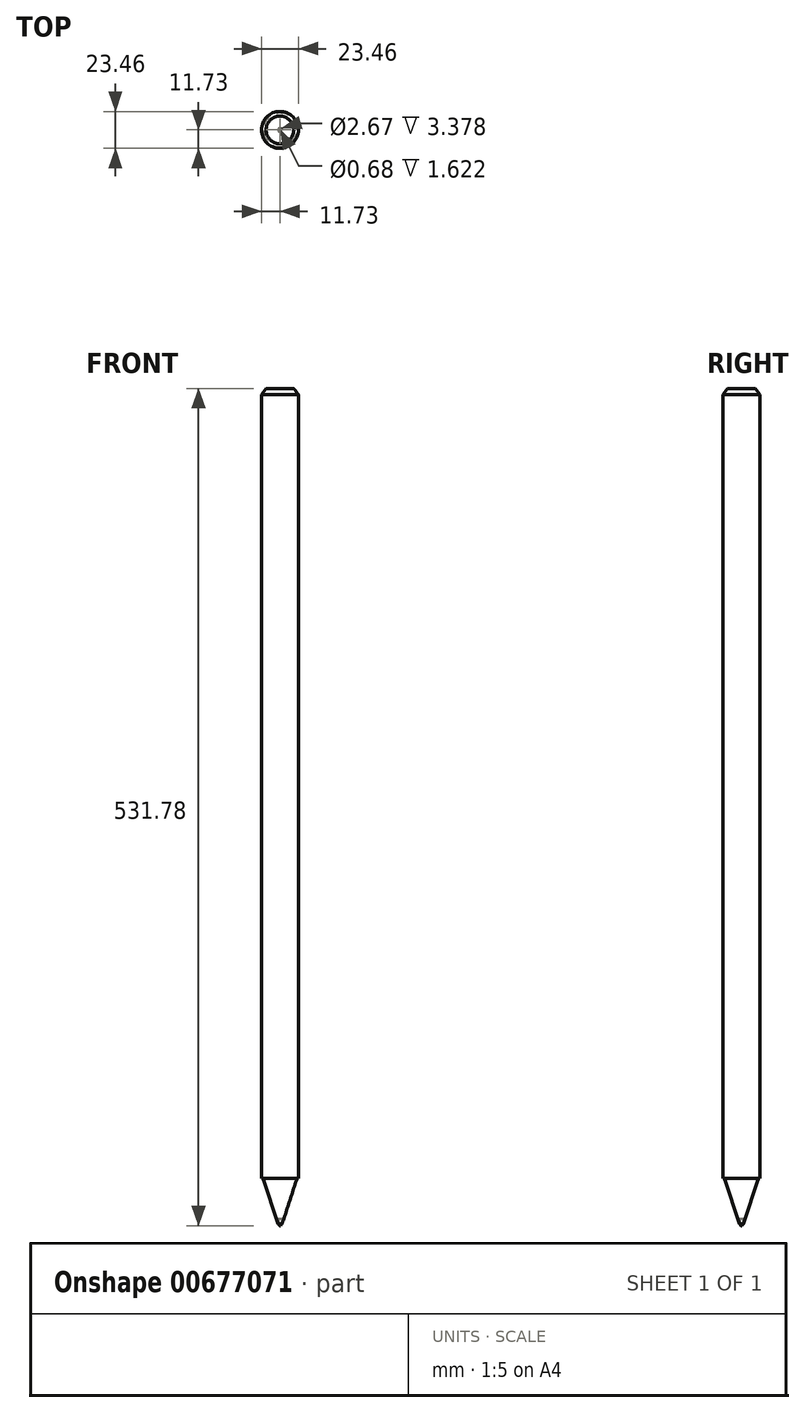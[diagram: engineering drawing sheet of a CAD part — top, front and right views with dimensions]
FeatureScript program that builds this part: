
annotation { "Feature Type Name" : "Feature", "Feature Type Description" : "" }
export const myFeature = defineFeature(function(context is Context, id is Id, definition is map)
    precondition{}
    {
        {
            var Q0;
            Q0=qCreatedBy(makeId("Front.planeOp"),FACE);
            var sketch = newSketch(context, id + "F0", { "sketchPlane" : qUnion([Q0])});
            skLineSegment(sketch, "E0", {"start": v(0, 241.42) * mm, "end": v(0, -256.53) * mm, "construction": true});
            skLineSegment(sketch, "E1", {"start": v(0, 241.42) * mm, "end": v(11.73, 241.42) * mm});
            skLineSegment(sketch, "E2", {"start": v(11.73, 241.42) * mm, "end": v(11.73, -256.53) * mm});
            skLineSegment(sketch, "E3", {"start": v(11.73, -256.53) * mm, "end": v(0, -256.53) * mm});
            skLineSegment(sketch, "E4", {"start": v(0, -256.53) * mm, "end": v(0, 241.42) * mm});
            skSolve(sketch);
        }
        {
            var Q0;
            Q0 = qSketchRegion(id + "F0", true);
            var Q1;
            Q1=sQuery(id+"F0.wireOp",EDGE,"E4");
            revolve(context, id + "F1", {"entities" : qUnion([Q0]), "axis" : qUnion([Q1]), "revolveType" : RevolveType.FULL});
        }
        {
            var Q0;
            Q0=qCreatedBy(makeId("Front.planeOp"),FACE);
            var sketch = newSketch(context, id + "F2", { "sketchPlane" : qUnion([Q0])});
            skLineSegment(sketch, "E5", {"start": v(0, 278.62) * mm, "end": v(0, -307.6) * mm, "construction": true});
            skLineSegment(sketch, "E6", {"start": v(-11, -255.85) * mm, "end": v(-1.33, -285.5) * mm});
            skLineSegment(sketch, "E7", {"start": v(-1.33, -285.5) * mm, "end": v(1.33, -285.5) * mm});
            skLineSegment(sketch, "E8", {"start": v(1.33, -285.5) * mm, "end": v(11.3, -256) * mm});
            skLineSegment(sketch, "E9", {"start": v(11.3, -256) * mm, "end": v(-11, -255.85) * mm});
            skLineSegment(sketch, "E10", {"start": v(0, -255.93) * mm, "end": v(0, -285.5) * mm});
            skSolve(sketch);
        }
        {
            var Q0;
            {var subQ0=sQuery(id+"F2.wireOp",EDGE,"E6");Q0=makeQuery(id+"F2.imprint","IMPRINT",FACE,{"disambiguationData":[TD([[makeQuery(id+"F2.imprint","IMPRINT",EDGE,{"derivedFrom":subQ0}),1.0]])]});}
            var Q1;
            Q1=sQuery(id+"F2.wireOp",EDGE,"E10");
            revolve(context, id + "F3", {"operationType" : NewBodyOperationType.ADD, "entities" : qUnion([Q0]), "axis" : qUnion([Q1]), "revolveType" : RevolveType.FULL});
        }
        {
            var Q0;
            Q0=qCreatedBy(makeId("Front.planeOp"),FACE);
            var sketch = newSketch(context, id + "F4", { "sketchPlane" : qUnion([Q0])});
            skLineSegment(sketch, "E11", {"start": v(0, -214.3) * mm, "end": v(0, -295.62) * mm, "construction": true});
            skLineSegment(sketch, "E12", {"start": v(-1, -285.25) * mm, "end": v(0, -287.14) * mm});
            skLineSegment(sketch, "E13", {"start": v(-1, -285.25) * mm, "end": v(0, -285.25) * mm});
            skLineSegment(sketch, "E14", {"start": v(0, -285.25) * mm, "end": v(0, -287.14) * mm});
            skSolve(sketch);
        }
        {
            var Q0;
            Q0 = qSketchRegion(id + "F4", true);
            var Q1;
            Q1=sQuery(id+"F4.wireOp",EDGE,"E14");
            revolve(context, id + "F5", {"operationType" : NewBodyOperationType.ADD, "entities" : qUnion([Q0]), "axis" : qUnion([Q1]), "revolveType" : RevolveType.FULL});
        }
        {
            var Q0;
            Q0=makeQuery(id+"F3.opRevolve","SWEPT_FACE",FACE,{"disambiguationData":[OSD([sQuery(id+"F2.wireOp",EDGE,"E7")])]});
            extrude(context, id + "F6", {"entities" : qUnion([Q0]), "operationType" : NewBodyOperationType.REMOVE, "oppositeDirection" : true, "depth" : 3.38 * mm, "offsetDistance" : 25.4 * mm});
        }
        {
            var Q0;
            Q0=qCreatedBy(makeId("Front.planeOp"),FACE);
            var sketch = newSketch(context, id + "F7", { "sketchPlane" : qUnion([Q0])});
            skLineSegment(sketch, "E15", {"start": v(0, 300.1) * mm, "end": v(0, 172.54) * mm, "construction": true});
            skLineSegment(sketch, "E16", {"start": v(11.72, 241.43) * mm, "end": v(8.78, 245.28) * mm});
            skLineSegment(sketch, "E17", {"start": v(8.78, 245.28) * mm, "end": v(0, 245.28) * mm});
            skLineSegment(sketch, "E18", {"start": v(0, 245.28) * mm, "end": v(0, 241.43) * mm});
            skLineSegment(sketch, "E19", {"start": v(0, 241.43) * mm, "end": v(11.72, 241.43) * mm});
            skSolve(sketch);
        }
        {
            var Q0;
            Q0 = qSketchRegion(id + "F7", true);
            var Q1;
            Q1=sQuery(id+"F7.wireOp",EDGE,"E18");
            revolve(context, id + "F8", {"operationType" : NewBodyOperationType.ADD, "entities" : qUnion([Q0]), "axis" : qUnion([Q1]), "revolveType" : RevolveType.FULL});
        }
        {
            var Q0;
            Q0=qCreatedBy(makeId("Right.planeOp"),FACE);
            var sketch = newSketch(context, id + "F9", { "sketchPlane" : qUnion([Q0])});
            skLineSegment(sketch, "E20", {"start": v(-0.6, -286.5) * mm, "end": v(0.6, -286.5) * mm});
            skLineSegment(sketch, "E21", {"start": v(0.6, -286.5) * mm, "end": v(0.6, -287.36) * mm});
            skLineSegment(sketch, "E22", {"start": v(0.6, -287.36) * mm, "end": v(-0.6, -287.36) * mm});
            skLineSegment(sketch, "E23", {"start": v(-0.6, -287.36) * mm, "end": v(-0.6, -286.5) * mm});
            skSolve(sketch);
        }
        {
            var Q0;
            Q0 = qSketchRegion(id + "F9", true);
            extrude(context, id + "F10", {"entities" : qUnion([Q0]), "operationType" : NewBodyOperationType.REMOVE, "endBound" : BoundingType.SYMMETRIC, "oppositeDirection" : true, "depth" : 25.4 * mm, "offsetDistance" : 25.4 * mm});
        }
        {
            var Q0;
            Q0=makeQuery(id+"F10.boolean.opBoolean","COPY",FACE,{"derivedFrom":makeQuery(id+"F10.opExtrude","SWEPT_FACE",FACE,{"disambiguationData":[OSD([sQuery(id+"F9.wireOp",EDGE,"E20")])]})});
            extrude(context, id + "F11", {"entities" : qUnion([Q0]), "operationType" : NewBodyOperationType.REMOVE, "oppositeDirection" : true, "depth" : 1.62 * mm, "offsetDistance" : 25.4 * mm});
        }
    });
